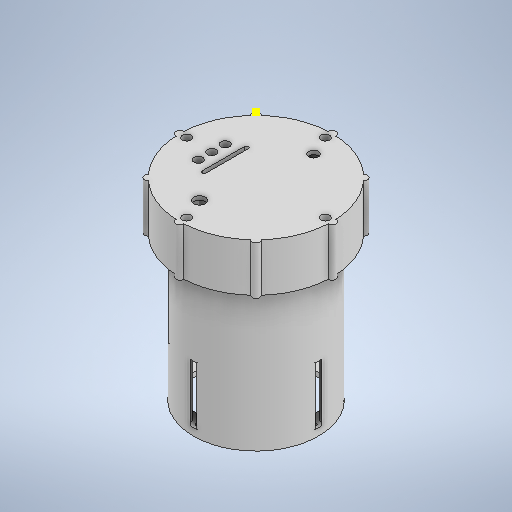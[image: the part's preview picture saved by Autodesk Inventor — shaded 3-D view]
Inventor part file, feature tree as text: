
AUTODESK INVENTOR PART (.ipt)
format: ipt  version: 2025.2 (Build 292293000, 293)  size: 2,184,704 bytes
history: native  units: in
note: dims shown in document units (in); Inventor stores cm internally (conversion verified against a paired STEP export)
features: extrude x46, sketch x13, projected_geometry x13, chamfer x8, other x6, fillet x6, mirror x3, pattern_circular x3, plane x3, helix x1
ambient origin geometry x8: Origin, YZ Plane, XZ Plane, XY Plane, X Axis, Y Axis, Z Axis, Center Point
bodies: Body1 (feature_tree), Body2 (feature_tree), Body3 (feature_tree), Body4 (feature_tree), Body5 (feature_tree)
feature tree (102):
  other  "BatteryCage"
  sketch  "Sketch1"  dims[d0=2.5748in d1=0.0098in]
  extrude  "Extrusion1"  Depth=0.0098in
  extrude  "Extrusion2"  Depth=0.4724in
  extrude  "Extrusion3"  Depth=0.0984in
  fillet  "Fillet1"  Radius=0.1969in
  chamfer  "Chamfer1"  Distance=0.0984in
  fillet  "Fillet2"  Radius=0.1181in
  extrude  "Extrusion4"  Depth=0.0197in
  chamfer  "Chamfer2"  Distance=0.0787in Angle=45.0deg
  sketch  "Sketch4"  dims[d8=0.7874in]
  extrude  "Extrusion6"  Depth=0.1181in TaperAngle=0.0deg
  mirror  "Mirror1"
  extrude  "Extrusion7"  Depth=0.0787in
  extrude  "Extrusion9"  Depth=0.5906in TaperAngle=0.0deg
  chamfer  "Chamfer4"  Distance=0.0512in
  extrude  "Extrusion10"  Depth=0.0787in
  fillet  "Fillet3"  Radius=0.0984in
  extrude  "Extrusion11"  Depth=0.0787in
  extrude  "Extrusion12"  Depth=0.0787in TaperAngle=45.0deg
  extrude  "Extrusion13"  Depth=0.0984in
  extrude  "Extrusion14"  Depth=0.0984in
  chamfer  "Chamfer5"  Distance=2.0472in
  extrude  "Extrusion15"  Depth=0.0787in
  extrude  "Extrusion16"  Depth=0.0787in TaperAngle=0.0deg
  extrude  "Extrusion17"  Depth=0.0787in TaperAngle=0.0deg
  extrude  "Extrusion18"  Depth=0.0787in
  extrude  "Extrusion19"  TaperAngle=0.0deg  [1 undecoded]
  pattern_circular  "Circular Pattern1"  [2 undecoded]
  extrude  "Extrusion20"  Depth=0.0787in
  pattern_circular  "Circular Pattern2"  [2 undecoded]
  helix  "Coil1"  [1 undecoded]
  extrude  "Extrusion21"  TaperAngle=0.0deg  [1 undecoded]
  extrude  "Extrusion22"  Depth=0.0787in
  extrude  "Extrusion23"  Depth=0.0787in
  extrude  "Extrusion24"  Depth=0.0787in
  chamfer  "Chamfer6"  Distance=0.9843in
  extrude  "Sensor Tower Base"  Depth=0.0787in TaperAngle=45.0deg
  extrude  "Extrusion27"  Depth=0.0787in TaperAngle=0.0deg
  extrude  "Extrusion28"  Depth=0.0787in
  extrude  "Extrusion34"  Depth=0.0787in
  extrude  "Extrusion35"  Depth=0.0787in
  extrude  "Extrusion36"  TaperAngle=0.0deg  [1 undecoded]
  extrude  "Extrusion44"  Depth=0.0787in
  extrude  "Extrusion37"  Depth=0.0787in
  extrude  "Extrusion38"  Depth=0.0787in
  mirror  "Mirror2"
  extrude  "Extrusion39"  TaperAngle=0.0deg  [1 undecoded]
  extrude  "Extrusion40"  Depth=0.0787in
  extrude  "Extrusion41"  TaperAngle=0.0deg  [1 undecoded]
  mirror  "Mirror3"
  chamfer  "Chamfer9"  Distance=0.1732in
  extrude  "Extrusion29"  Depth=0.0787in
  extrude  "Extrusion30"  Depth=0.0787in TaperAngle=0.0deg
  extrude  "Extrusion31"  Depth=0.0787in TaperAngle=360.0deg
  chamfer  "Chamfer7"  Distance=0.1575in
  extrude  "Extrusion32"  Depth=0.0787in TaperAngle=0.0deg
  pattern_circular  "Circular Pattern3"  Count=8 Angle=360.0deg
  extrude  "O-ring Gland"  Depth=0.0787in
  fillet  "Fillet4"  Radius=0.185in
  plane  "Work Plane2"
  extrude  "Extrusion47"  Depth=0.0787in
  chamfer  "Chamfer8"  Distance=0.0787in
  extrude  "Start of Camera"  Depth=0.0787in
  fillet  "Fillet5"  Radius=0.1457in
  extrude  "Extrusion43"  Depth=0.3937in
  plane  "Work Plane1"
  extrude  "Extrusion45"  Depth=0.3937in TaperAngle=0.0deg
  extrude  "Extrusion46"  Depth=0.0787in
  fillet  "Fillet6"  [1 undecoded]
  plane  "Work Plane3"
  extrude  "Extrusion48"  Depth=0.3937in TaperAngle=0.0deg
  extrude  "Extrusion50"  Depth=0.0787in
  projected_geometry  "Projected Loop1"
  projected_geometry  "Projected Loop2"
  other  "StartOfPiCage"
  other  "PiCage"
  projected_geometry  "Projected Loop3"
  sketch  "Sketch10"  dims[d9=0.1969in d10=0.0984in d11=0.0in d12=0.1181in]
  projected_geometry  "Projected Loop4"
  sketch  "Sketch17"  dims[d13=0.3937in d14=0.0in d15=0.0197in d16=0.0512in d17=0.0787in d18=45.0deg]
  projected_geometry  "Projected Loop5"
  other  "SensorTower"
  projected_geometry  "Projected Loop6"
  other  "SensorCover"
  sketch  "Sketch33"  dims[d19=0.1181in d20=4.4724in d21=0.0in]
  projected_geometry  "Projected Loop7"
  projected_geometry  "Projected Loop8"
  projected_geometry  "Projected Loop9"
  projected_geometry  "Projected Loop10"
  projected_geometry  "Projected Loop11"
  sketch  "Sketch35"  dims[d22=0.0512in d23=0.0787in d24=45.0deg d25=0.0512in]
  projected_geometry  "Projected Loop12"
  other  "Camera"
  sketch  "Sketch39"  dims[d31=0.1732in d32=0.5906in d33=0.0in]
  sketch  "Sketch40"  dims[d34=0.0512in]
  sketch  "Sketch43"  dims[d35=0.0512in]
  sketch  "Sketch44"  dims[d36=0.0512in]
  projected_geometry  "Projected Loop13"
  sketch  "Sketch Rectangular Pattern1"  dims[d2=2.0512in d3=0.4724in]
  sketch  "Sketch Rectangular Pattern2"  dims[d4=0.0984in d5=0.0in d6=0.0079in d7=0.1969in]
  sketch  "Sketch45"  dims[d37=0.0in d38=0.0512in d41=0.1339in d42=0.0984in d43=0.0in d44=0.0512in d45=0.0787in d46=45.0deg d47=0.0984in d48=0.0984in d49=2.0472in d50=0.2756in d51=2.9528in d52=0.0in d53=1.1811in d54=0.0in d55=0.5669in d56=0.0in d57=0.8661in d58=0.0787in d59=0.6299in d60=0.0984in d61=0.0in d62=0.1772in d63=0.2756in d64=0.0172in d65=0.9843in d66=0.0in d67=0.9843in d68=0.0787in d69=45.0deg d70=0.1969in d71=0.0in d72=0.7874in d73=0.5906in d74=0.5669in d75=0.0in d76=3.1181in d77=0.1122in d78=0.2756in d79=0.0in d80=0.7087in d81=0.0in d82=0.1732in d83=1.4173in d84=0.2362in d85=0.0in d86=1.5748in d87=360.0deg d89=0.1575in d90=0.2756in d91=0.0in d92=3.1496in d93=360.0deg d95=2.4016in d96=0.185in d97=0.1102in d98=0.0787in d99=1.4016in d100=0.1457in d101=0.3937in d102=0.9449in d103=0.0in d104=90.0deg d105=90.0deg d106=0.0in d107=0.0in d108=0.3937in d109=0.0in d110=0.2362in d111=0.0in d112=0.3937in d113=0.0in d114=0.2756in d115=0.2756in d116=0.3937in d117=0.0in d118=0.0768in d119=0.0787in d120=45.0deg d122=0.315in d126=0.1417in d127=0.1181in d128=0.0in d129=2.126in d130=0.2953in d131=1.378in d132=0.0in d133=1.4961in d134=1.3386in d135=0.0709in d136=0.1969in d137=0.9843in d138=0.0in d139=0.2756in d140=0.0787in d141=2.126in d142=0.1969in d143=0.2756in d144=0.1181in d145=0.0in d146=0.1969in d147=1.378in d148=0.0in d149=1.2992in d150=0.1181in d151=0.0in d152=0.4134in d153=0.0787in d154=45.0deg d155=0.9449in d156=0.0787in d157=0.2362in d158=0.0in d159=2.3622in d160=360.0deg d162=1.4173in d163=0.1496in d164=0.0689in d165=0.0in d167=0.1181in d168=0.0787in d169=0.0787in d170=45.0deg d171=1.0079in d172=1.0in d173=0.0197in d174=0.0591in d175=0.0591in d176=0.3937in d177=0.0in d178=0.4724in d179=0.0in d180=0.0787in d181=0.0787in d182=0.4724in d183=0.0in d184=0.2756in d185=0.5118in d186=0.0in d187=45.0deg d188=0.0591in d189=0.5512in d190=0.0in d191=0.0472in d192=30.0deg d193=0.0315in d194=0.0787in d195=0.0787in d196=0.0in d197=0.5512in d198=1.2008in d199=0.0in d200=0.063in d201=45.0deg d202=30.0deg d203=0.1181in d204=0.0945in d205=1.2008in d206=0.0in d207=1.4961in d208=0.0984in d209=0.063in d210=0.0in d211=0.0394in d212=1.1772in d213=0.689in d214=0.0in d215=0.0276in d216=0.0in d217=0.0787in d218=0.1378in d219=0.3937in d220=0.126in d221=0.0in d222=0.7835in d223=0.3937in d224=0.0in d225=0.3858in d226=0.0787in d227=0.0787in d228=45.0deg d229=-0.0236in d230=0.1575in d231=0.748in d232=0.3937in d233=0.0in d234=-0.0787in d235=0.0394in d236=0.0394in d237=0.0394in d238=0.0394in d239=0.0787in d240=1.1811in d242=0.7874in d243=1.1811in d245=0.7874in d248=0.7874in d249=0.7874in d251=0.7874in d252=0.3937in d254=0.3937in d256=0.0591in d257=0.685in d258=0.0in d259=0.1969in d262=0.1969in d263=0.2362in d264=0.0787in d265=0.0in]
note: 11 required parameter values undecoded (feature->parameter linkage not recoverable at this tier; creation-order binding heuristic only, values carry confidence <= 0.55)
